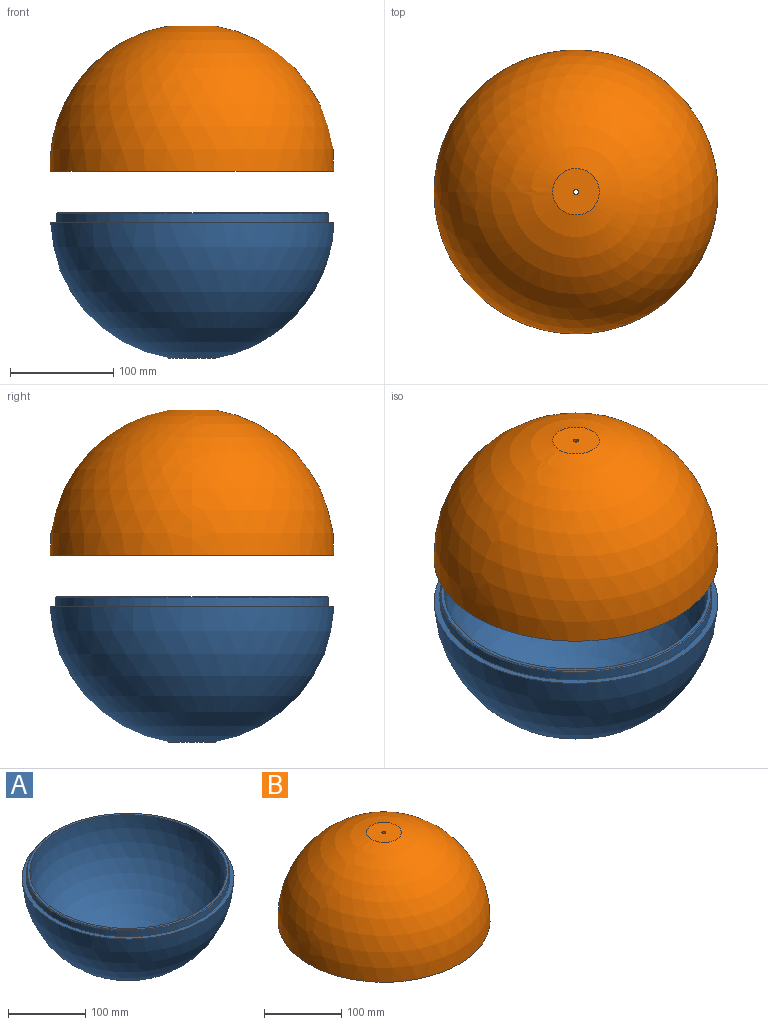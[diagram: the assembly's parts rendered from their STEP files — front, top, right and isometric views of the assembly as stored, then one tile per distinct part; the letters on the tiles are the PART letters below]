
ASSEMBLY  parts=2 mates=1
PART A: 8 faces, bbox 274.8x274.8x140.6 mm
  f0: sphere r=127.5mm, area 106126.1mm2, adj f1,f7
  f1: plane 261.5x261.5mm, normal (0,0,1), area 2715.3mm2, adj f0,f6
  f2: cylinder r=131.75mm len=263.5mm, axis (0,0,1), area 7450.3mm2, adj f3,f6
  f3: plane 274.82x274.82mm, normal (0,0,1), area 4785.2mm2, adj f2,f4
  f4: sphere r=137.5mm, area 112870.6mm2, adj f3,f5
  f5: plane 45x45mm, normal (0,0,-1), area 1570mm2, adj f4,f7
  f6: cone r=130.75mm half-angle=45deg, axis (0,0,-1), area 1166.3mm2, adj f1,f2
  f7: cylinder r=2.55mm len=8.17mm, axis (0,0,-1), area 131.1mm2, adj f0,f5
PART B: 8 faces, bbox 275x275x140.6 mm
  f0: sphere r=127.5mm, area 98115mm2, adj f1,f6
  f1: plane 266.5x266.5mm, normal (0,0,-1), area 4788.8mm2, adj f0,f5
  f2: plane 45x45mm, normal (0,0,1), area 1570mm2, adj f3,f6
  f3: sphere r=137.5mm, area 121509.9mm2, adj f2,f4
  f4: plane 274.82x274.82mm, normal (0,0,-1), area 2696.1mm2, adj f3,f7
  f5: cylinder r=133.25mm len=266.5mm, axis (0,0,-1), area 7535.1mm2, adj f1,f7
  f6: cylinder r=2.55mm len=8.17mm, axis (0,0,1), area 131.1mm2, adj f0,f2
  f7: cone r=133.25mm half-angle=45deg, axis (0,0,-1), area 1188.5mm2, adj f4,f5
PLACE A t=(0,0,-50)mm
PLACE B at identity
MATE revolute A.f2 <-> B.f5  axis (0,0,1) through (0,0,-50)mm
